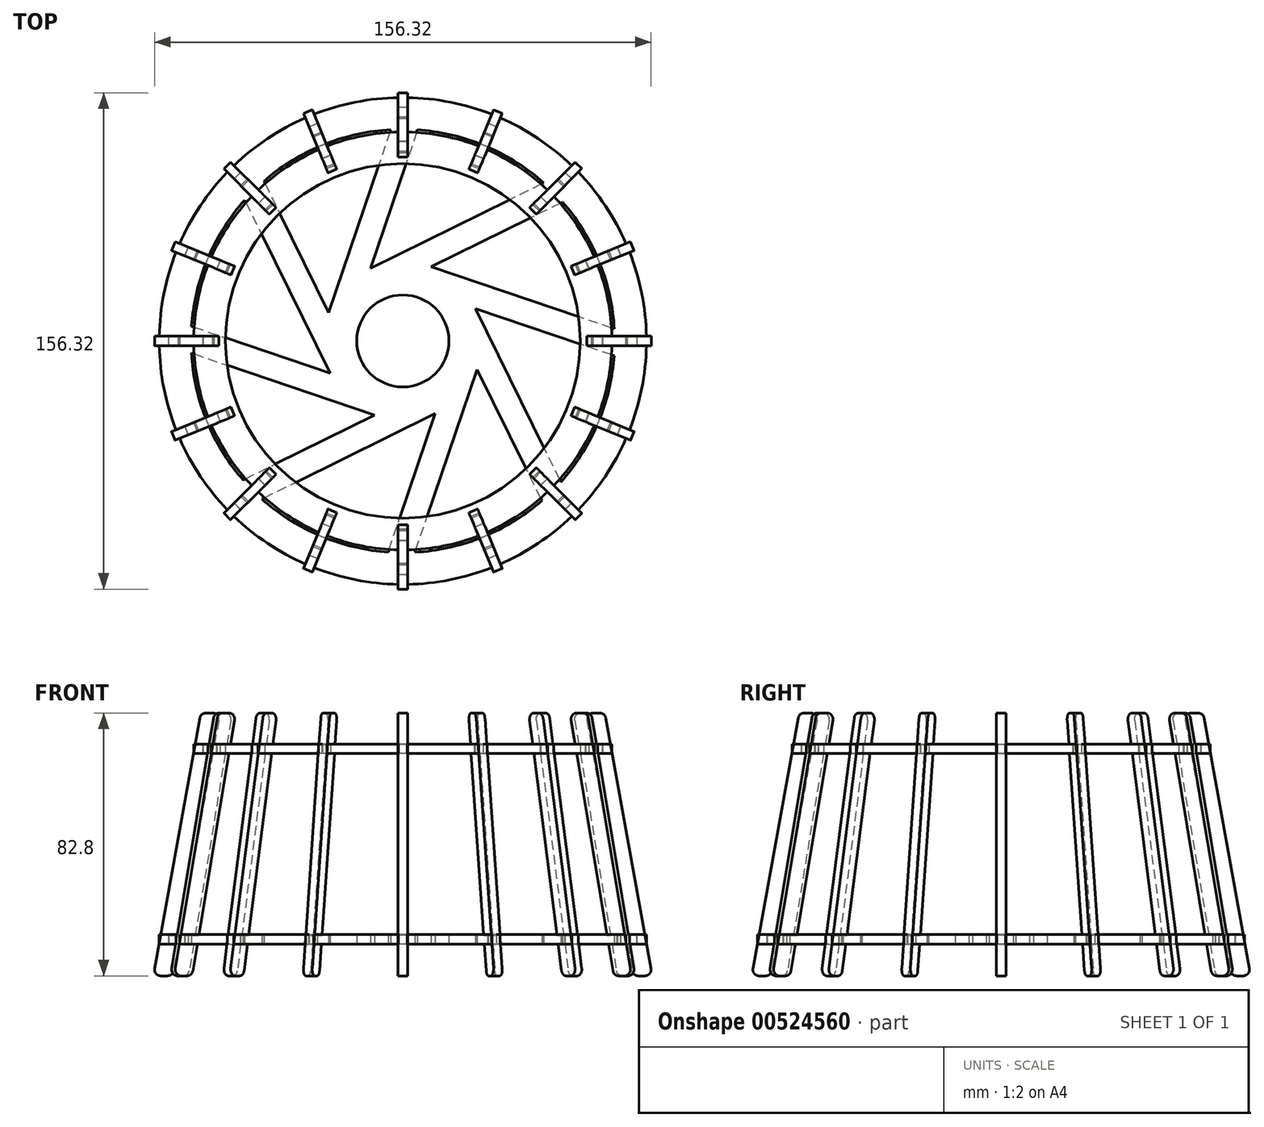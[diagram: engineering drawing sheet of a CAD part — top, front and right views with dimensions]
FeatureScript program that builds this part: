
annotation { "Feature Type Name" : "Feature", "Feature Type Description" : "" }
export const myFeature = defineFeature(function(context is Context, id is Id, definition is map)
    precondition{}
    {
        {
            var Q0;
            Q0=qCreatedBy(makeId("Top.planeOp"),FACE);
            cPlane(context, id + "F0", {"entities" : qUnion([Q0]), "cplaneType" : CPlaneType.OFFSET, "offset" : 60 * mm, "oppositeDirection" : true, "width" : 150 * mm, "height" : 150 * mm});
        }
        {
            var Q0;
            Q0=qCreatedBy(makeId("Top.planeOp"),FACE);
            var sketch = newSketch(context, id + "F1", { "sketchPlane" : qUnion([Q0])});
            skCircle(sketch, "E0", {"center": v(0, 0) * mm, "radius": 55.83 * mm});
            skArc(sketch, "E1", {"start": v(-65.82, -1.4) * mm, "mid": v(-64.57, -12.84) * mm, "end": v(-61.34, -23.9) * mm});
            skLineSegment(sketch, "E2", {"start": v(-65.82, 1.4) * mm, "end": v(-62.82, 1.4) * mm});
            skLineSegment(sketch, "E3", {"start": v(-62.82, 1.4) * mm, "end": v(-62.82, -1.4) * mm});
            skLineSegment(sketch, "E4", {"start": v(-62.82, -1.4) * mm, "end": v(-65.82, -1.4) * mm});
            skLineSegment(sketch, "E5.1.0", {"start": v(-61.34, -23.9) * mm, "end": v(-58.57, -22.75) * mm});
            skLineSegment(sketch, "E5.1.1", {"start": v(-58.57, -22.75) * mm, "end": v(-57.5, -25.33) * mm});
            skLineSegment(sketch, "E5.1.2", {"start": v(-57.5, -25.33) * mm, "end": v(-60.27, -26.48) * mm});
            skLineSegment(sketch, "E5.2.0", {"start": v(-47.53, -45.55) * mm, "end": v(-45.4, -43.43) * mm});
            skLineSegment(sketch, "E5.2.1", {"start": v(-45.4, -43.43) * mm, "end": v(-43.43, -45.4) * mm});
            skLineSegment(sketch, "E5.2.2", {"start": v(-43.43, -45.4) * mm, "end": v(-45.55, -47.53) * mm});
            skLineSegment(sketch, "E5.3.0", {"start": v(-26.48, -60.27) * mm, "end": v(-25.33, -57.5) * mm});
            skLineSegment(sketch, "E5.3.1", {"start": v(-25.33, -57.5) * mm, "end": v(-22.75, -58.57) * mm});
            skLineSegment(sketch, "E5.3.2", {"start": v(-22.75, -58.57) * mm, "end": v(-23.9, -61.34) * mm});
            skLineSegment(sketch, "E5.4.0", {"start": v(-1.4, -65.82) * mm, "end": v(-1.4, -62.82) * mm});
            skLineSegment(sketch, "E5.4.1", {"start": v(-1.4, -62.82) * mm, "end": v(1.4, -62.82) * mm});
            skLineSegment(sketch, "E5.4.2", {"start": v(1.4, -62.82) * mm, "end": v(1.4, -65.82) * mm});
            skLineSegment(sketch, "E5.5.0", {"start": v(23.9, -61.34) * mm, "end": v(22.75, -58.57) * mm});
            skLineSegment(sketch, "E5.5.1", {"start": v(22.75, -58.57) * mm, "end": v(25.33, -57.5) * mm});
            skLineSegment(sketch, "E5.5.2", {"start": v(25.33, -57.5) * mm, "end": v(26.48, -60.27) * mm});
            skLineSegment(sketch, "E5.6.0", {"start": v(45.55, -47.53) * mm, "end": v(43.43, -45.4) * mm});
            skLineSegment(sketch, "E5.6.1", {"start": v(43.43, -45.4) * mm, "end": v(45.4, -43.43) * mm});
            skLineSegment(sketch, "E5.6.2", {"start": v(45.4, -43.43) * mm, "end": v(47.53, -45.55) * mm});
            skLineSegment(sketch, "E5.7.0", {"start": v(60.27, -26.48) * mm, "end": v(57.5, -25.33) * mm});
            skLineSegment(sketch, "E5.7.1", {"start": v(57.5, -25.33) * mm, "end": v(58.57, -22.75) * mm});
            skLineSegment(sketch, "E5.7.2", {"start": v(58.57, -22.75) * mm, "end": v(61.34, -23.9) * mm});
            skLineSegment(sketch, "E5.8.0", {"start": v(65.82, -1.4) * mm, "end": v(62.82, -1.4) * mm});
            skLineSegment(sketch, "E5.8.1", {"start": v(62.82, -1.4) * mm, "end": v(62.82, 1.4) * mm});
            skLineSegment(sketch, "E5.8.2", {"start": v(62.82, 1.4) * mm, "end": v(65.82, 1.4) * mm});
            skLineSegment(sketch, "E5.9.0", {"start": v(61.34, 23.9) * mm, "end": v(58.57, 22.75) * mm});
            skLineSegment(sketch, "E5.9.1", {"start": v(58.57, 22.75) * mm, "end": v(57.5, 25.33) * mm});
            skLineSegment(sketch, "E5.9.2", {"start": v(57.5, 25.33) * mm, "end": v(60.27, 26.48) * mm});
            skLineSegment(sketch, "E5.10.0", {"start": v(47.53, 45.55) * mm, "end": v(45.4, 43.43) * mm});
            skLineSegment(sketch, "E5.10.1", {"start": v(45.4, 43.43) * mm, "end": v(43.43, 45.4) * mm});
            skLineSegment(sketch, "E5.10.2", {"start": v(43.43, 45.4) * mm, "end": v(45.55, 47.53) * mm});
            skLineSegment(sketch, "E5.11.0", {"start": v(26.48, 60.27) * mm, "end": v(25.33, 57.5) * mm});
            skLineSegment(sketch, "E5.11.1", {"start": v(25.33, 57.5) * mm, "end": v(22.75, 58.57) * mm});
            skLineSegment(sketch, "E5.11.2", {"start": v(22.75, 58.57) * mm, "end": v(23.9, 61.34) * mm});
            skLineSegment(sketch, "E5.12.0", {"start": v(1.4, 65.82) * mm, "end": v(1.4, 62.82) * mm});
            skLineSegment(sketch, "E5.12.1", {"start": v(1.4, 62.82) * mm, "end": v(-1.4, 62.82) * mm});
            skLineSegment(sketch, "E5.12.2", {"start": v(-1.4, 62.82) * mm, "end": v(-1.4, 65.82) * mm});
            skLineSegment(sketch, "E5.13.0", {"start": v(-23.9, 61.34) * mm, "end": v(-22.75, 58.57) * mm});
            skLineSegment(sketch, "E5.13.1", {"start": v(-22.75, 58.57) * mm, "end": v(-25.33, 57.5) * mm});
            skLineSegment(sketch, "E5.13.2", {"start": v(-25.33, 57.5) * mm, "end": v(-26.48, 60.27) * mm});
            skLineSegment(sketch, "E5.14.0", {"start": v(-45.55, 47.53) * mm, "end": v(-43.43, 45.4) * mm});
            skLineSegment(sketch, "E5.14.1", {"start": v(-43.43, 45.4) * mm, "end": v(-45.4, 43.43) * mm});
            skLineSegment(sketch, "E5.14.2", {"start": v(-45.4, 43.43) * mm, "end": v(-47.53, 45.55) * mm});
            skLineSegment(sketch, "E5.15.0", {"start": v(-60.27, 26.48) * mm, "end": v(-57.5, 25.33) * mm});
            skLineSegment(sketch, "E5.15.1", {"start": v(-57.5, 25.33) * mm, "end": v(-58.57, 22.75) * mm});
            skLineSegment(sketch, "E5.15.2", {"start": v(-58.57, 22.75) * mm, "end": v(-61.34, 23.9) * mm});
            skArc(sketch, "E6.trimOffspring", {"start": v(-61.34, 23.9) * mm, "mid": v(-64.57, 12.84) * mm, "end": v(-65.82, 1.4) * mm});
            skArc(sketch, "E7.trimOffspring", {"start": v(-47.53, 45.55) * mm, "mid": v(-54.74, 36.57) * mm, "end": v(-60.27, 26.48) * mm});
            skArc(sketch, "E8.trimOffspring", {"start": v(-26.48, 60.27) * mm, "mid": v(-36.57, 54.74) * mm, "end": v(-45.55, 47.53) * mm});
            skArc(sketch, "E9.trimOffspring", {"start": v(-1.4, 65.82) * mm, "mid": v(-12.84, 64.57) * mm, "end": v(-23.9, 61.34) * mm});
            skArc(sketch, "E10.trimOffspring", {"start": v(23.9, 61.34) * mm, "mid": v(12.84, 64.57) * mm, "end": v(1.4, 65.82) * mm});
            skArc(sketch, "E11.trimOffspring", {"start": v(45.55, 47.53) * mm, "mid": v(36.57, 54.74) * mm, "end": v(26.48, 60.27) * mm});
            skArc(sketch, "E12.trimOffspring", {"start": v(60.27, 26.48) * mm, "mid": v(54.74, 36.57) * mm, "end": v(47.53, 45.55) * mm});
            skArc(sketch, "E13.trimOffspring", {"start": v(65.82, 1.4) * mm, "mid": v(64.57, 12.84) * mm, "end": v(61.34, 23.9) * mm});
            skArc(sketch, "E14.trimOffspring", {"start": v(61.34, -23.9) * mm, "mid": v(64.57, -12.84) * mm, "end": v(65.82, -1.4) * mm});
            skArc(sketch, "E15.trimOffspring", {"start": v(47.53, -45.55) * mm, "mid": v(54.74, -36.57) * mm, "end": v(60.27, -26.48) * mm});
            skArc(sketch, "E16.trimOffspring", {"start": v(26.48, -60.27) * mm, "mid": v(36.57, -54.74) * mm, "end": v(45.55, -47.53) * mm});
            skArc(sketch, "E17.trimOffspring", {"start": v(1.4, -65.82) * mm, "mid": v(12.84, -64.57) * mm, "end": v(23.9, -61.34) * mm});
            skArc(sketch, "E18.trimOffspring", {"start": v(-23.9, -61.34) * mm, "mid": v(-12.84, -64.57) * mm, "end": v(-1.4, -65.82) * mm});
            skArc(sketch, "E19.trimOffspring", {"start": v(-45.55, -47.53) * mm, "mid": v(-36.57, -54.74) * mm, "end": v(-26.48, -60.27) * mm});
            skArc(sketch, "E20.trimOffspring", {"start": v(-60.27, -26.48) * mm, "mid": v(-54.74, -36.57) * mm, "end": v(-47.53, -45.55) * mm});
            skSolve(sketch);
        }
        {
            var Q0;
            Q0=qSketchRegion(id+"F1",true);
            extrude(context, id + "F2", {"entities" : qUnion([Q0]), "depth" : 3 * mm});
        }
        {
            var Q0;
            Q0=qCreatedBy(id+"F0.planeOp",FACE);
            var sketch = newSketch(context, id + "F3", { "sketchPlane" : qUnion([Q0])});
            skArc(sketch, "E21", {"start": v(-76.65, -1.4) * mm, "mid": v(-75.2, -14.96) * mm, "end": v(-71.36, -28.04) * mm});
            skArc(sketch, "E22.trimOffspring", {"start": v(-71.36, 28.04) * mm, "mid": v(-75.2, 14.96) * mm, "end": v(-76.65, 1.4) * mm});
            skArc(sketch, "E23.trimOffspring", {"start": v(-55.2, 53.21) * mm, "mid": v(-63.75, 42.6) * mm, "end": v(-70.28, 30.63) * mm});
            skArc(sketch, "E24.trimOffspring", {"start": v(-30.63, 70.28) * mm, "mid": v(-42.6, 63.75) * mm, "end": v(-53.21, 55.2) * mm});
            skArc(sketch, "E25.trimOffspring", {"start": v(-1.4, 76.65) * mm, "mid": v(-14.96, 75.2) * mm, "end": v(-28.04, 71.36) * mm});
            skArc(sketch, "E26.trimOffspring", {"start": v(28.04, 71.36) * mm, "mid": v(14.96, 75.2) * mm, "end": v(1.4, 76.65) * mm});
            skArc(sketch, "E27.trimOffspring", {"start": v(53.21, 55.2) * mm, "mid": v(42.6, 63.75) * mm, "end": v(30.63, 70.28) * mm});
            skArc(sketch, "E28.trimOffspring", {"start": v(70.28, 30.63) * mm, "mid": v(63.75, 42.6) * mm, "end": v(55.2, 53.21) * mm});
            skArc(sketch, "E29.trimOffspring", {"start": v(76.65, 1.4) * mm, "mid": v(75.2, 14.96) * mm, "end": v(71.36, 28.04) * mm});
            skArc(sketch, "E30.trimOffspring", {"start": v(71.36, -28.04) * mm, "mid": v(75.2, -14.96) * mm, "end": v(76.65, -1.4) * mm});
            skArc(sketch, "E31.trimOffspring", {"start": v(55.2, -53.21) * mm, "mid": v(63.75, -42.6) * mm, "end": v(70.28, -30.63) * mm});
            skArc(sketch, "E32.trimOffspring", {"start": v(30.63, -70.28) * mm, "mid": v(42.6, -63.75) * mm, "end": v(53.21, -55.2) * mm});
            skArc(sketch, "E33.trimOffspring", {"start": v(1.4, -76.65) * mm, "mid": v(14.96, -75.2) * mm, "end": v(28.04, -71.36) * mm});
            skArc(sketch, "E34.trimOffspring", {"start": v(-28.04, -71.36) * mm, "mid": v(-14.96, -75.2) * mm, "end": v(-1.4, -76.65) * mm});
            skArc(sketch, "E35.trimOffspring", {"start": v(-53.21, -55.2) * mm, "mid": v(-42.6, -63.75) * mm, "end": v(-30.63, -70.28) * mm});
            skArc(sketch, "E36.trimOffspring", {"start": v(-70.28, -30.63) * mm, "mid": v(-63.75, -42.6) * mm, "end": v(-55.2, -53.21) * mm});
            skLineSegment(sketch, "E37", {"start": v(-76.65, -1.4) * mm, "end": v(-73.65, -1.4) * mm});
            skLineSegment(sketch, "E38", {"start": v(-73.65, -1.4) * mm, "end": v(-73.65, 1.4) * mm});
            skLineSegment(sketch, "E39", {"start": v(-76.65, 1.4) * mm, "end": v(-73.65, 1.4) * mm});
            skLineSegment(sketch, "E40.1.0", {"start": v(-71.36, -28.04) * mm, "end": v(-68.58, -26.9) * mm});
            skLineSegment(sketch, "E40.1.1", {"start": v(-67.51, -29.48) * mm, "end": v(-68.58, -26.9) * mm});
            skLineSegment(sketch, "E40.1.2", {"start": v(-70.28, -30.63) * mm, "end": v(-67.51, -29.48) * mm});
            skLineSegment(sketch, "E40.2.0", {"start": v(-55.2, -53.21) * mm, "end": v(-53.07, -51.1) * mm});
            skLineSegment(sketch, "E40.2.1", {"start": v(-51.1, -53.07) * mm, "end": v(-53.07, -51.1) * mm});
            skLineSegment(sketch, "E40.2.2", {"start": v(-53.21, -55.2) * mm, "end": v(-51.1, -53.07) * mm});
            skLineSegment(sketch, "E40.3.0", {"start": v(-30.63, -70.28) * mm, "end": v(-29.48, -67.51) * mm});
            skLineSegment(sketch, "E40.3.1", {"start": v(-26.9, -68.58) * mm, "end": v(-29.48, -67.51) * mm});
            skLineSegment(sketch, "E40.3.2", {"start": v(-28.04, -71.36) * mm, "end": v(-26.9, -68.58) * mm});
            skLineSegment(sketch, "E40.4.0", {"start": v(-1.4, -76.65) * mm, "end": v(-1.4, -73.65) * mm});
            skLineSegment(sketch, "E40.4.1", {"start": v(1.4, -73.65) * mm, "end": v(-1.4, -73.65) * mm});
            skLineSegment(sketch, "E40.4.2", {"start": v(1.4, -76.65) * mm, "end": v(1.4, -73.65) * mm});
            skLineSegment(sketch, "E40.5.0", {"start": v(28.04, -71.36) * mm, "end": v(26.9, -68.58) * mm});
            skLineSegment(sketch, "E40.5.1", {"start": v(29.48, -67.51) * mm, "end": v(26.9, -68.58) * mm});
            skLineSegment(sketch, "E40.5.2", {"start": v(30.63, -70.28) * mm, "end": v(29.48, -67.51) * mm});
            skLineSegment(sketch, "E40.6.0", {"start": v(53.21, -55.2) * mm, "end": v(51.1, -53.07) * mm});
            skLineSegment(sketch, "E40.6.1", {"start": v(53.07, -51.1) * mm, "end": v(51.1, -53.07) * mm});
            skLineSegment(sketch, "E40.6.2", {"start": v(55.2, -53.21) * mm, "end": v(53.07, -51.1) * mm});
            skLineSegment(sketch, "E40.7.0", {"start": v(70.28, -30.63) * mm, "end": v(67.51, -29.48) * mm});
            skLineSegment(sketch, "E40.7.1", {"start": v(68.58, -26.9) * mm, "end": v(67.51, -29.48) * mm});
            skLineSegment(sketch, "E40.7.2", {"start": v(71.36, -28.04) * mm, "end": v(68.58, -26.9) * mm});
            skLineSegment(sketch, "E40.8.0", {"start": v(76.65, -1.4) * mm, "end": v(73.65, -1.4) * mm});
            skLineSegment(sketch, "E40.8.1", {"start": v(73.65, 1.4) * mm, "end": v(73.65, -1.4) * mm});
            skLineSegment(sketch, "E40.8.2", {"start": v(76.65, 1.4) * mm, "end": v(73.65, 1.4) * mm});
            skLineSegment(sketch, "E40.9.0", {"start": v(71.36, 28.04) * mm, "end": v(68.58, 26.9) * mm});
            skLineSegment(sketch, "E40.9.1", {"start": v(67.51, 29.48) * mm, "end": v(68.58, 26.9) * mm});
            skLineSegment(sketch, "E40.9.2", {"start": v(70.28, 30.63) * mm, "end": v(67.51, 29.48) * mm});
            skLineSegment(sketch, "E40.10.0", {"start": v(55.2, 53.21) * mm, "end": v(53.07, 51.1) * mm});
            skLineSegment(sketch, "E40.10.1", {"start": v(51.1, 53.07) * mm, "end": v(53.07, 51.1) * mm});
            skLineSegment(sketch, "E40.10.2", {"start": v(53.21, 55.2) * mm, "end": v(51.1, 53.07) * mm});
            skLineSegment(sketch, "E40.11.0", {"start": v(30.63, 70.28) * mm, "end": v(29.48, 67.51) * mm});
            skLineSegment(sketch, "E40.11.1", {"start": v(26.9, 68.58) * mm, "end": v(29.48, 67.51) * mm});
            skLineSegment(sketch, "E40.11.2", {"start": v(28.04, 71.36) * mm, "end": v(26.9, 68.58) * mm});
            skLineSegment(sketch, "E40.12.0", {"start": v(1.4, 76.65) * mm, "end": v(1.4, 73.65) * mm});
            skLineSegment(sketch, "E40.12.1", {"start": v(-1.4, 73.65) * mm, "end": v(1.4, 73.65) * mm});
            skLineSegment(sketch, "E40.12.2", {"start": v(-1.4, 76.65) * mm, "end": v(-1.4, 73.65) * mm});
            skLineSegment(sketch, "E40.13.0", {"start": v(-28.04, 71.36) * mm, "end": v(-26.9, 68.58) * mm});
            skLineSegment(sketch, "E40.13.1", {"start": v(-29.48, 67.51) * mm, "end": v(-26.9, 68.58) * mm});
            skLineSegment(sketch, "E40.13.2", {"start": v(-30.63, 70.28) * mm, "end": v(-29.48, 67.51) * mm});
            skLineSegment(sketch, "E40.14.0", {"start": v(-53.21, 55.2) * mm, "end": v(-51.1, 53.07) * mm});
            skLineSegment(sketch, "E40.14.1", {"start": v(-53.07, 51.1) * mm, "end": v(-51.1, 53.07) * mm});
            skLineSegment(sketch, "E40.14.2", {"start": v(-55.2, 53.21) * mm, "end": v(-53.07, 51.1) * mm});
            skLineSegment(sketch, "E40.15.0", {"start": v(-70.28, 30.63) * mm, "end": v(-67.51, 29.48) * mm});
            skLineSegment(sketch, "E40.15.1", {"start": v(-68.58, 26.9) * mm, "end": v(-67.51, 29.48) * mm});
            skLineSegment(sketch, "E40.15.2", {"start": v(-71.36, 28.04) * mm, "end": v(-68.58, 26.9) * mm});
            skCircle(sketch, "E41", {"center": v(0, 0) * mm, "radius": 14.5 * mm});
            skArc(sketch, "E42", {"start": v(-44.37, -49.76) * mm, "mid": v(-25.89, -61.44) * mm, "end": v(-4.62, -66.5) * mm});
            skLineSegment(sketch, "E43", {"start": v(44.37, 49.76) * mm, "end": v(-10.2, 22.85) * mm});
            skLineSegment(sketch, "E44.0", {"start": v(50.3, 43.76) * mm, "end": v(8.92, 23.35) * mm});
            skLineSegment(sketch, "E45.1.0", {"start": v(4.62, 66.5) * mm, "end": v(-10.2, 22.82) * mm});
            skLineSegment(sketch, "E45.1.1", {"start": v(-3.8, 66.56) * mm, "end": v(-23.37, 8.94) * mm});
            skLineSegment(sketch, "E45.2.0", {"start": v(-43.76, 50.3) * mm, "end": v(-23.35, 8.92) * mm});
            skLineSegment(sketch, "E45.2.1", {"start": v(-49.76, 44.37) * mm, "end": v(-22.85, -10.2) * mm});
            skLineSegment(sketch, "E45.3.0", {"start": v(-66.5, 4.62) * mm, "end": v(-22.82, -10.2) * mm});
            skLineSegment(sketch, "E45.3.1", {"start": v(-66.56, -3.8) * mm, "end": v(-8.94, -23.37) * mm});
            skLineSegment(sketch, "E45.4.0", {"start": v(-50.3, -43.76) * mm, "end": v(-8.92, -23.35) * mm});
            skLineSegment(sketch, "E45.4.1", {"start": v(-44.37, -49.76) * mm, "end": v(10.2, -22.85) * mm});
            skLineSegment(sketch, "E45.5.0", {"start": v(-4.62, -66.5) * mm, "end": v(10.2, -22.82) * mm});
            skLineSegment(sketch, "E45.5.1", {"start": v(3.8, -66.56) * mm, "end": v(23.37, -8.94) * mm});
            skLineSegment(sketch, "E45.6.0", {"start": v(43.76, -50.3) * mm, "end": v(23.35, -8.92) * mm});
            skLineSegment(sketch, "E45.6.1", {"start": v(49.76, -44.37) * mm, "end": v(22.85, 10.2) * mm});
            skLineSegment(sketch, "E45.7.0", {"start": v(66.5, -4.62) * mm, "end": v(22.82, 10.2) * mm});
            skLineSegment(sketch, "E45.7.1", {"start": v(66.56, 3.8) * mm, "end": v(8.94, 23.37) * mm});
            skPoint(sketch, "E46.orphan", {"position": v(-23.67, 8.04) * mm});
            skPoint(sketch, "E47.orphan", {"position": v(-11.06, 22.42) * mm});
            skPoint(sketch, "E48.orphan", {"position": v(8.04, 23.67) * mm});
            skPoint(sketch, "E49.orphan", {"position": v(-22.42, -11.06) * mm});
            skPoint(sketch, "E50.orphan", {"position": v(22.42, 11.06) * mm});
            skPoint(sketch, "E51.orphan", {"position": v(-8.04, -23.67) * mm});
            skArc(sketch, "E52.trimOffspring", {"start": v(3.8, -66.56) * mm, "mid": v(25.14, -61.75) * mm, "end": v(43.76, -50.3) * mm});
            skArc(sketch, "E53.trimOffspring", {"start": v(49.76, -44.37) * mm, "mid": v(61.44, -25.89) * mm, "end": v(66.5, -4.62) * mm});
            skArc(sketch, "E54.trimOffspring", {"start": v(66.56, 3.8) * mm, "mid": v(61.75, 25.14) * mm, "end": v(50.3, 43.76) * mm});
            skArc(sketch, "E55.trimOffspring", {"start": v(44.37, 49.76) * mm, "mid": v(25.89, 61.44) * mm, "end": v(4.62, 66.5) * mm});
            skArc(sketch, "E56.trimOffspring", {"start": v(-3.8, 66.56) * mm, "mid": v(-25.14, 61.75) * mm, "end": v(-43.76, 50.3) * mm});
            skArc(sketch, "E57.trimOffspring", {"start": v(-49.76, 44.37) * mm, "mid": v(-61.44, 25.89) * mm, "end": v(-66.5, 4.62) * mm});
            skArc(sketch, "E58.trimOffspring", {"start": v(-66.56, -3.8) * mm, "mid": v(-61.75, -25.14) * mm, "end": v(-50.3, -43.76) * mm});
            skSolve(sketch);
        }
        {
            var Q0;
            Q0=qSketchRegion(id+"F3",true);
            extrude(context, id + "F4", {"entities" : qUnion([Q0]), "depth" : 3 * mm});
        }
        {
            var Q0;
            Q0=qCreatedBy(makeId("Front.planeOp"),FACE);
            var sketch = newSketch(context, id + "F5", { "sketchPlane" : qUnion([Q0])});
            skLineSegment(sketch, "E59", {"start": v(-57.94, 10.44) * mm, "end": v(-59.32, 2.8) * mm});
            skLineSegment(sketch, "E60", {"start": v(-63.9, 11.16) * mm, "end": v(-78.13, -67.64) * mm});
            skLineSegment(sketch, "E61", {"start": v(-59.82, 0) * mm, "end": v(-62.82, 0) * mm});
            skLineSegment(sketch, "E62", {"start": v(-62.82, 0) * mm, "end": v(-62.82, 2.8) * mm});
            skLineSegment(sketch, "E63", {"start": v(-62.82, 2.8) * mm, "end": v(-59.32, 2.8) * mm});
            skLineSegment(sketch, "E64.trimOffspring", {"start": v(-59.82, 0) * mm, "end": v(-70.15, -57.2) * mm});
            skLineSegment(sketch, "E65", {"start": v(-70.65, -60) * mm, "end": v(-73.65, -60) * mm});
            skLineSegment(sketch, "E66", {"start": v(-73.65, -60) * mm, "end": v(-73.65, -57.2) * mm});
            skLineSegment(sketch, "E67", {"start": v(-73.65, -57.2) * mm, "end": v(-70.15, -57.2) * mm});
            skLineSegment(sketch, "E68.trimOffspring", {"start": v(-70.65, -60) * mm, "end": v(-72.16, -68.36) * mm});
            skLineSegment(sketch, "E69", {"start": v(-59.9, 12.8) * mm, "end": v(-61.94, 12.8) * mm});
            skPoint(sketch, "E70.visualSharp", {"position": v(-63.6, 12.8) * mm});
            skArc(sketch, "E70.filletArc", {"start": v(-61.94, 12.8) * mm, "mid": v(-63.22, 12.33) * mm, "end": v(-63.9, 11.16) * mm});
            skPoint(sketch, "E71.visualSharp", {"position": v(-57.5, 12.8) * mm});
            skArc(sketch, "E71.filletArc", {"start": v(-57.94, 10.44) * mm, "mid": v(-58.37, 12.08) * mm, "end": v(-59.9, 12.8) * mm});
            skLineSegment(sketch, "E72", {"start": v(-74.13, -70) * mm, "end": v(-76.16, -70) * mm});
            skPoint(sketch, "E73.visualSharp", {"position": v(-78.56, -70) * mm});
            skArc(sketch, "E73.filletArc", {"start": v(-78.13, -67.64) * mm, "mid": v(-77.7, -69.28) * mm, "end": v(-76.16, -70) * mm});
            skPoint(sketch, "E74.visualSharp", {"position": v(-72.46, -70) * mm});
            skArc(sketch, "E74.filletArc", {"start": v(-74.13, -70) * mm, "mid": v(-72.85, -69.53) * mm, "end": v(-72.16, -68.36) * mm});
            skSolve(sketch);
        }
        {
            var Q0;
            Q0=qSketchRegion(id+"F5",true);
            extrude(context, id + "F6", {"entities" : qUnion([Q0]), "endBound" : BoundingType.SYMMETRIC, "depth" : 3 * mm});
        }
        {
            var Q0;
            Q0=makeQuery(id+"F6.opExtrude","SWEPT_BODY",BODY,{"disambiguationData":[OSD([sQuery(id+"F5.wireOp",EDGE,"E59"),sQuery(id+"F5.wireOp",EDGE,"E60"),sQuery(id+"F5.wireOp",EDGE,"E61"),sQuery(id+"F5.wireOp",EDGE,"E62"),sQuery(id+"F5.wireOp",EDGE,"E63"),sQuery(id+"F5.wireOp",EDGE,"E64.trimOffspring"),sQuery(id+"F5.wireOp",EDGE,"E65"),sQuery(id+"F5.wireOp",EDGE,"E66"),sQuery(id+"F5.wireOp",EDGE,"E67"),sQuery(id+"F5.wireOp",EDGE,"E68.trimOffspring"),sQuery(id+"F5.wireOp",EDGE,"E69"),sQuery(id+"F5.wireOp",EDGE,"E70.filletArc"),sQuery(id+"F5.wireOp",EDGE,"E71.filletArc"),sQuery(id+"F5.wireOp",EDGE,"E72"),sQuery(id+"F5.wireOp",EDGE,"E73.filletArc"),sQuery(id+"F5.wireOp",EDGE,"E74.filletArc")])]});
            var Q1;
            Q1=sQuery(id+"F1.wireOp",EDGE,"E0");
            circularPattern(context, id + "F7", {"entities" : qUnion([Q0]), "axis" : qUnion([Q1]), "angle" : 360 * degree, "instanceCount" : 16, "equalSpace" : true});
        }
    });
